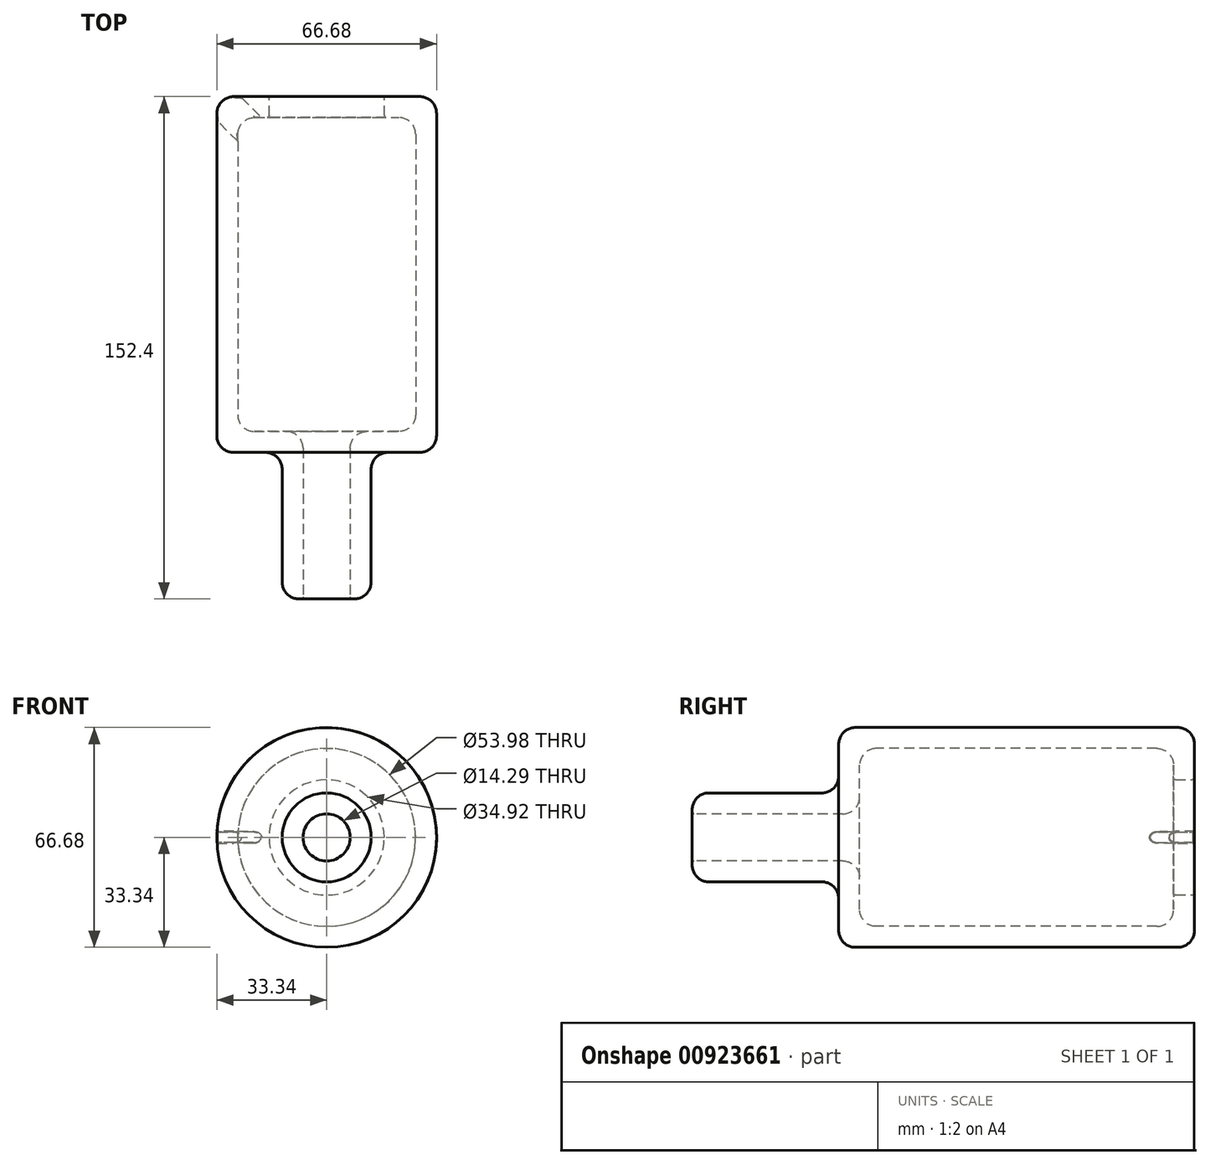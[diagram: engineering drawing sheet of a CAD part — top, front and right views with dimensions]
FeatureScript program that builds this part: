
annotation { "Feature Type Name" : "Feature", "Feature Type Description" : "" }
export const myFeature = defineFeature(function(context is Context, id is Id, definition is map)
    precondition{}
    {
        {
            var Q0;
            Q0=qCreatedBy(makeId("Right.planeOp"),FACE);
            var sketch = newSketch(context, id + "F0", { "sketchPlane" : qUnion([Q0])});
            skLineSegment(sketch, "E0", {"start": v(-76.2, 0) * mm, "end": v(76.2, 0) * mm});
            skLineSegment(sketch, "E1", {"start": v(-76.2, 0) * mm, "end": v(-76.2, 7.14) * mm});
            skLineSegment(sketch, "E2", {"start": v(-76.2, 7.14) * mm, "end": v(-25.4, 7.14) * mm});
            skLineSegment(sketch, "E3", {"start": v(-25.4, 7.14) * mm, "end": v(-25.4, 26.99) * mm});
            skLineSegment(sketch, "E4", {"start": v(-25.4, 26.99) * mm, "end": v(76.2, 26.99) * mm});
            skLineSegment(sketch, "E5", {"start": v(76.2, 26.99) * mm, "end": v(76.2, 0) * mm});
            skSolve(sketch);
        }
        {
            var Q0;
            Q0 = qSketchRegion(id + "F0", true);
            var Q1;
            Q1=sQuery(id+"F0.wireOp",EDGE,"E0");
            revolve(context, id + "F1", {"surfaceOperationType" : NewSurfaceOperationType.NEW, "entities" : qUnion([Q0]), "axis" : qUnion([Q1]), "revolveType" : RevolveType.FULL});
        }
        {
            var Q0;
            Q0=makeQuery(id+"F1.opRevolve","SWEPT_FACE",FACE,{"disambiguationData":[OSD([sQuery(id+"F0.wireOp",EDGE,"E5")])]});
            var Q1;
            Q1=makeQuery(id+"F1.opRevolve","SWEPT_FACE",FACE,{"disambiguationData":[OSD([sQuery(id+"F0.wireOp",EDGE,"E1")])]});
            shell(context, id + "F2", {"entities" : qUnion([Q0, Q1]), "thickness" : 6.35 * mm, "oppositeDirection" : true});
        }
        {
            var Q0;
            Q0=makeQuery(id+"F1.opRevolve","SWEPT_FACE",FACE,{"disambiguationData":[OSD([sQuery(id+"F0.wireOp",EDGE,"E5")])]});
            var sketch = newSketch(context, id + "F3", { "sketchPlane" : qUnion([Q0])});
            skCircle(sketch, "E6", {"center": v(0, 0) * mm, "radius": 17.46 * mm});
            skCircle(sketch, "E7.0", {"center": v(0, 0) * mm, "radius": 33.34 * mm});
            skSolve(sketch);
        }
        {
            var Q0;
            Q0 = qSketchRegion(id + "F3", true);
            extrude(context, id + "F4", {"entities" : qUnion([Q0]), "operationType" : NewBodyOperationType.ADD, "oppositeDirection" : true, "depth" : 6.35 * mm, "offsetDistance" : 25.4 * mm});
        }
        {
            var Q0;
            Q0=makeQuery(id+"F1.opRevolve","SWEPT_EDGE",EDGE,{"disambiguationData":[OSD([sQuery(id+"F0.wireOp",EDGE,"E4"),sQuery(id+"F0.wireOp",EDGE,"E5")])]});
            var Q1;
            Q1=makeQuery(id+"F1.opRevolve","SWEPT_EDGE",EDGE,{"disambiguationData":[OSD([sQuery(id+"F0.wireOp",EDGE,"E3"),sQuery(id+"F0.wireOp",EDGE,"E4")])]});
            var Q2;
            Q2=makeQuery(id+"F2.opShell","OFFSET_FACE",FACE,{"disambiguationData":[OSD([sQuery(id+"F0.wireOp",EDGE,"E4")])]});
            var Q3;
            Q3=makeQuery(id+"F1.opRevolve","SWEPT_FACE",FACE,{"disambiguationData":[OSD([sQuery(id+"F0.wireOp",EDGE,"E2")])]});
            var Q4;
            Q4=makeQuery(id+"F2.opShell","OFFSET_EDGE",EDGE,{"disambiguationData":[OSD([sQuery(id+"F0.wireOp",EDGE,"E2"),sQuery(id+"F0.wireOp",EDGE,"E3")])]});
            fillet(context, id + "F5", {"entities" : qUnion([Q0, Q1, Q2, Q3, Q4]), "radius" : 5.08 * mm, "tangentPropagation" : true, "allowEdgeOverflow" : false});
        }
        {
            var Q0;
            Q0=makeQuery(id+"F2.opShell","OFFSET_EDGE",EDGE,{"disambiguationData":[OSD([sQuery(id+"F0.wireOp",EDGE,"E1"),sQuery(id+"F0.wireOp",EDGE,"E2")])]});
            var Q1;
            Q1=makeQuery(id+"F4.opExtrude","SWEPT_FACE",FACE,{"disambiguationData":[OSD([sQuery(id+"F3.wireOp",EDGE,"E6")])]});
            fillet(context, id + "F6", {"entities" : qUnion([Q0, Q1]), "radius" : 0.64 * mm, "tangentPropagation" : true, "allowEdgeOverflow" : false});
        }
        {
            var Q0;
            Q0=qCreatedBy(makeId("Top.planeOp"),FACE);
            var sketch = newSketch(context, id + "F7", { "sketchPlane" : qUnion([Q0])});
            skLineSegment(sketch, "E8", {"start": v(-31.85, 74.71) * mm, "end": v(-41.27, 84.14) * mm});
            skLineSegment(sketch, "E9", {"start": v(-31.85, 74.71) * mm, "end": v(-40.7, 65.86) * mm});
            skArc(sketch, "E10", {"start": v(-28.26, 76.2) * mm, "mid": v(-31.85, 74.71) * mm, "end": v(-33.34, 71.12) * mm, "construction": true});
            skSolve(sketch);
        }
        {
            var Q0;
            Q0=sQuery(id+"F7.wireOp",EDGE,"E8");
            var Q1;
            Q1=sQuery(id+"F7.wireOp",VERTEX,"E8.end");
            cPlane(context, id + "F8", {"entities" : qUnion([Q0, Q1]), "cplaneType" : CPlaneType.LINE_POINT, "offset" : 25.4 * mm, "width" : 152.4 * mm, "height" : 152.4 * mm});
        }
        {
            var Q0;
            Q0=qCreatedBy(id+"F8.planeOp",FACE);
            var sketch = newSketch(context, id + "F9", { "sketchPlane" : qUnion([Q0])});
            skLineSegment(sketch, "E11.bottom", {"start": v(-35.39, -1.59) * mm, "end": v(-25.23, -1.59) * mm});
            skLineSegment(sketch, "E11.top", {"start": v(-35.39, 1.59) * mm, "end": v(-25.23, 1.59) * mm});
            skLineSegment(sketch, "E11.left", {"start": v(-35.39, -1.59) * mm, "end": v(-35.39, 1.59) * mm});
            skLineSegment(sketch, "E11.right", {"start": v(-25.23, -1.59) * mm, "end": v(-25.23, 1.59) * mm});
            skPoint(sketch, "E11.middle", {"position": v(-30.3, 0) * mm});
            skSolve(sketch);
        }
        {
            var Q0;
            Q0 = qSketchRegion(id + "F9", true);
            extrude(context, id + "F10", {"entities" : qUnion([Q0]), "operationType" : NewBodyOperationType.REMOVE, "oppositeDirection" : true, "depth" : 42.93 * mm, "offsetDistance" : 25.4 * mm});
        }
        {
            var Q0;
            Q0=makeQuery(id+"F10.boolean.opBoolean","COPY",EDGE,{"derivedFrom":makeQuery(id+"F10.opExtrude","SWEPT_EDGE",EDGE,{"disambiguationData":[OSD([sQuery(id+"F9.wireOp",EDGE,"E11.top"),sQuery(id+"F9.wireOp",EDGE,"E11.right")])]})});
            var Q1;
            Q1=makeQuery(id+"F10.boolean.opBoolean","COPY",EDGE,{"derivedFrom":makeQuery(id+"F10.opExtrude","SWEPT_EDGE",EDGE,{"disambiguationData":[OSD([sQuery(id+"F9.wireOp",EDGE,"E11.bottom"),sQuery(id+"F9.wireOp",EDGE,"E11.right")])]})});
            var Q2;
            Q2=makeQuery(id+"F10.boolean.opBoolean","COPY",EDGE,{"derivedFrom":makeQuery(id+"F10.opExtrude","SWEPT_EDGE",EDGE,{"disambiguationData":[OSD([sQuery(id+"F9.wireOp",EDGE,"E11.top"),sQuery(id+"F9.wireOp",EDGE,"E11.left")])]})});
            var Q3;
            Q3=makeQuery(id+"F10.boolean.opBoolean","COPY",EDGE,{"derivedFrom":makeQuery(id+"F10.opExtrude","SWEPT_EDGE",EDGE,{"disambiguationData":[OSD([sQuery(id+"F9.wireOp",EDGE,"E11.bottom"),sQuery(id+"F9.wireOp",EDGE,"E11.left")])]})});
            fillet(context, id + "F11", {"entities" : qUnion([Q0, Q1, Q2, Q3]), "radius" : 1.59 * mm, "tangentPropagation" : true, "allowEdgeOverflow" : false});
        }
        {
            var Q0;
            Q0=makeQuery(id+"F10.boolean.opBoolean","INTERSECT",EDGE,{"derivedFrom":[makeQuery(id+"F5.opFillet","BLEND_FACE",FACE,{"disambiguationData":[OSD([sQuery(id+"F0.wireOp",EDGE,"E4"),sQuery(id+"F3.wireOp",EDGE,"E6"),sQuery(id+"F3.wireOp",EDGE,"E7.0")])]}),makeQuery(id+"F10.opExtrude","SWEPT_FACE",FACE,{"disambiguationData":[OSD([sQuery(id+"F9.wireOp",EDGE,"E11.top")])]})]});
            var Q1;
            Q1=makeQuery(id+"F10.boolean.opBoolean","INTERSECT",EDGE,{"derivedFrom":[makeQuery(id+"F5.opFillet","BLEND_FACE",FACE,{"disambiguationData":[OSD([sQuery(id+"F0.wireOp",EDGE,"E4"),sQuery(id+"F0.wireOp",EDGE,"E5")])]}),makeQuery(id+"F10.opExtrude","SWEPT_FACE",FACE,{"disambiguationData":[OSD([sQuery(id+"F9.wireOp",EDGE,"E11.top")])]})]});
            fillet(context, id + "F12", {"entities" : qUnion([Q0, Q1]), "radius" : 0.25 * mm, "tangentPropagation" : true, "allowEdgeOverflow" : false});
        }
    });
